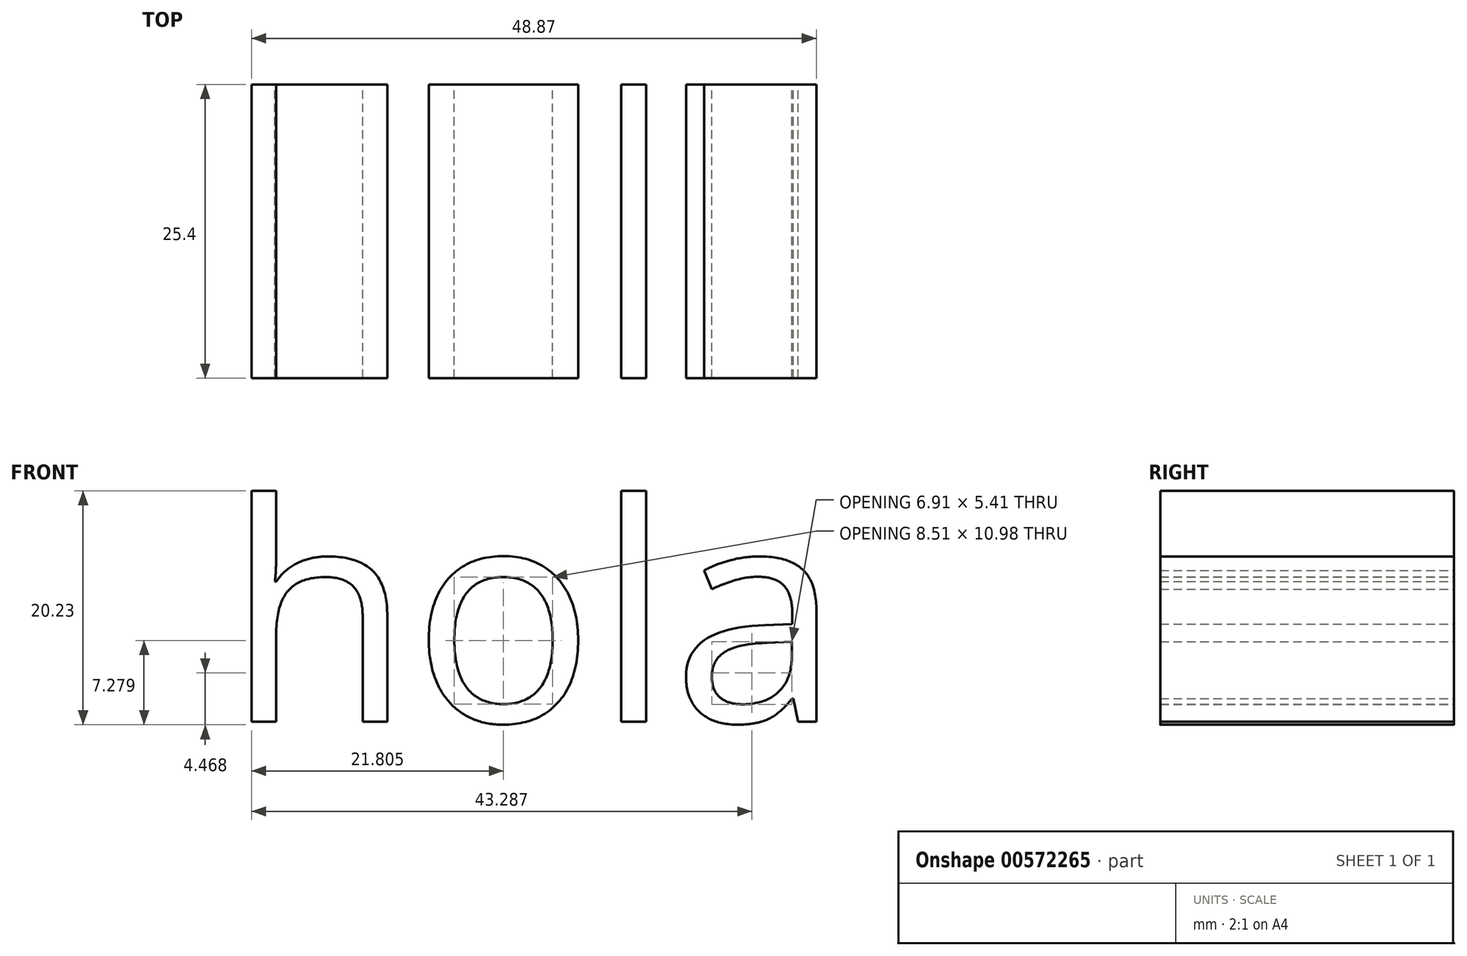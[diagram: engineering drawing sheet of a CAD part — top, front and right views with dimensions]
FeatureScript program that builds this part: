
annotation { "Feature Type Name" : "Feature", "Feature Type Description" : "" }
export const myFeature = defineFeature(function(context is Context, id is Id, definition is map)
    precondition{}
    {
        {
            var Q0;
            Q0=qCreatedBy(makeId("Front.planeOp"),FACE);
            var sketch = newSketch(context, id + "F0", { "sketchPlane" : qUnion([Q0])});
            skText(sketch, "E0", { "text": "hola", "fontName": "OpenSans-Regular.ttf"});
            const initialGuessF0  = {"E0": [0, 0, 1, 0, 0.01892]};
            skSetInitialGuess(sketch, initialGuessF0);
            skSolve(sketch);
        }
        {
            var Q0;
            Q0 = qSketchRegion(id + "F0", true);
            extrude(context, id + "F1", {"entities" : qUnion([Q0]), "depth" : 25.4 * mm, "offsetDistance" : 25.4 * mm});
        }
    });
